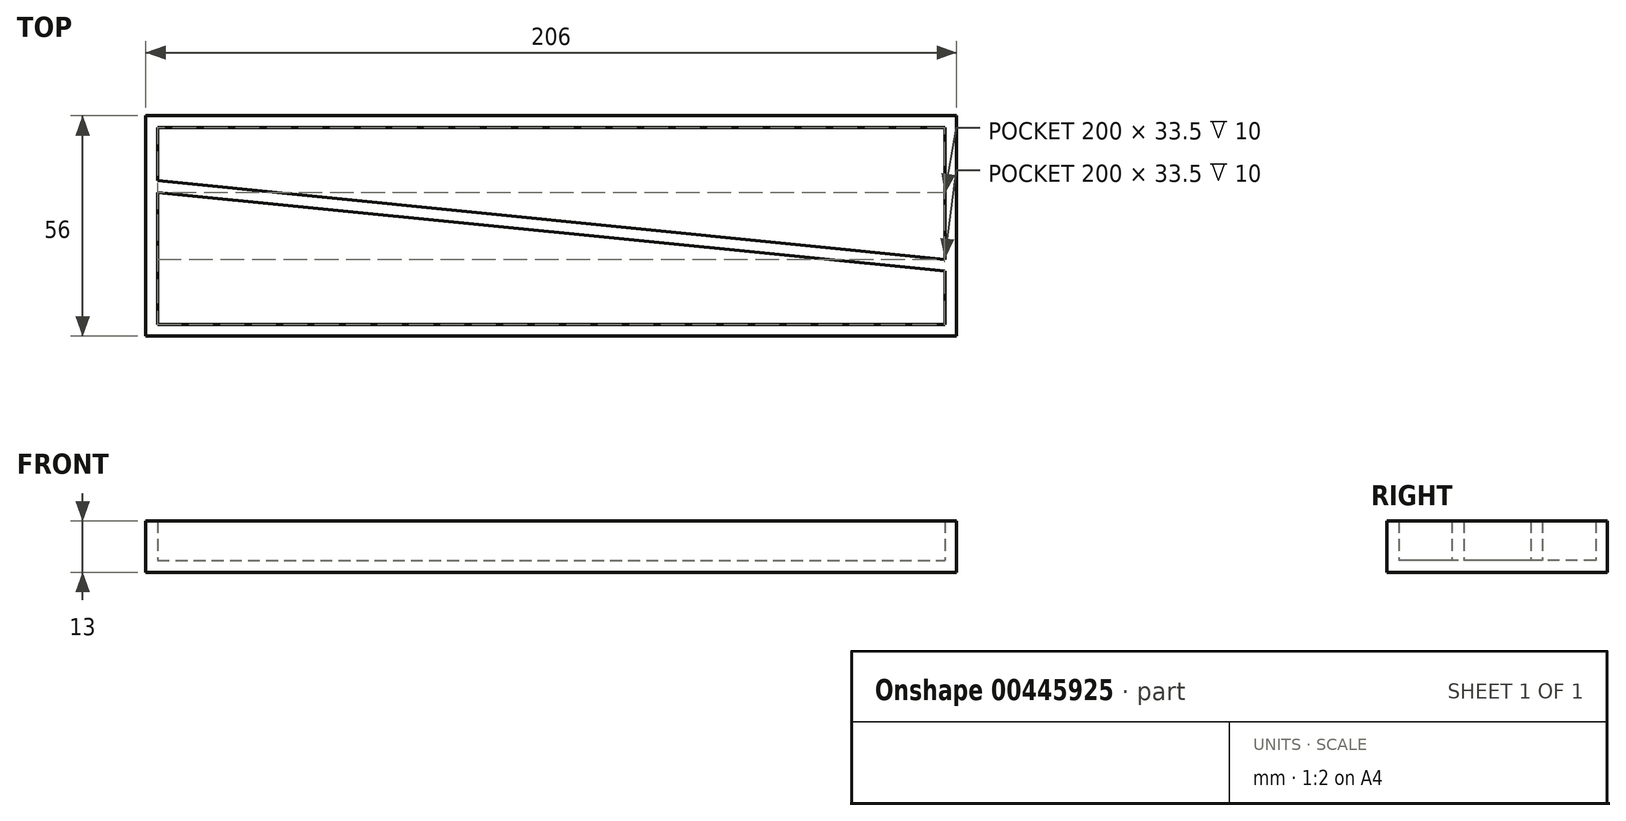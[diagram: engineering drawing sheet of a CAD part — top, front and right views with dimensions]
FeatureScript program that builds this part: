
annotation { "Feature Type Name" : "Feature", "Feature Type Description" : "" }
export const myFeature = defineFeature(function(context is Context, id is Id, definition is map)
    precondition{}
    {
        {
            var Q0;
            Q0=qCreatedBy(makeId("Top.planeOp"),FACE);
            var sketch = newSketch(context, id + "F0", { "sketchPlane" : qUnion([Q0])});
            skLineSegment(sketch, "E0.bottom", {"start": v(-103, 28) * mm, "end": v(103, 28) * mm});
            skLineSegment(sketch, "E0.top", {"start": v(-103, -28) * mm, "end": v(103, -28) * mm});
            skLineSegment(sketch, "E0.left", {"start": v(-103, 28) * mm, "end": v(-103, -28) * mm});
            skLineSegment(sketch, "E0.right", {"start": v(103, 28) * mm, "end": v(103, -28) * mm});
            skSolve(sketch);
        }
        {
            var Q0;
            Q0 = qSketchRegion(id + "F0", true);
            extrude(context, id + "F1", {"entities" : qUnion([Q0]), "depth" : 3 * mm});
        }
        {
            var Q0;
            Q0=makeQuery(id+"F1.opExtrude","CAP_FACE",FACE,{"disambiguationData":[OSD([sQuery(id+"F0.wireOp",EDGE,"E0.bottom"),sQuery(id+"F0.wireOp",EDGE,"E0.top"),sQuery(id+"F0.wireOp",EDGE,"E0.left"),sQuery(id+"F0.wireOp",EDGE,"E0.right")])],"isStart":false});
            var sketch = newSketch(context, id + "F2", { "sketchPlane" : qUnion([Q0])});
            skLineSegment(sketch, "E1.bottom", {"start": v(-103, 28) * mm, "end": v(103, 28) * mm});
            skLineSegment(sketch, "E1.top", {"start": v(-103, -28) * mm, "end": v(103, -28) * mm});
            skLineSegment(sketch, "E1.left", {"start": v(-103, 28) * mm, "end": v(-103, -28) * mm});
            skLineSegment(sketch, "E1.right", {"start": v(103, 28) * mm, "end": v(103, -28) * mm});
            skLineSegment(sketch, "E2.bottom", {"start": v(-100, 25) * mm, "end": v(100, 25) * mm});
            skLineSegment(sketch, "E2.top", {"start": v(-100, -25) * mm, "end": v(100, -25) * mm});
            skLineSegment(sketch, "E2.left", {"start": v(-100, 25) * mm, "end": v(-100, 11.5) * mm});
            skLineSegment(sketch, "E2.right", {"start": v(100, 25) * mm, "end": v(100, -8.5) * mm});
            skLineSegment(sketch, "E3", {"start": v(-100, 8.5) * mm, "end": v(100, -11.5) * mm});
            skLineSegment(sketch, "E4", {"start": v(-100, 11.5) * mm, "end": v(100, -8.5) * mm});
            skLineSegment(sketch, "E5", {"start": v(-100, 8.5) * mm, "end": v(-100, -25) * mm});
            skLineSegment(sketch, "E6", {"start": v(100, -11.5) * mm, "end": v(100, -25) * mm});
            skSolve(sketch);
        }
        {
            var Q0;
            Q0 = qSketchRegion(id + "F2", true);
            extrude(context, id + "F3", {"entities" : qUnion([Q0]), "operationType" : NewBodyOperationType.ADD, "depth" : 10 * mm});
        }
    });
